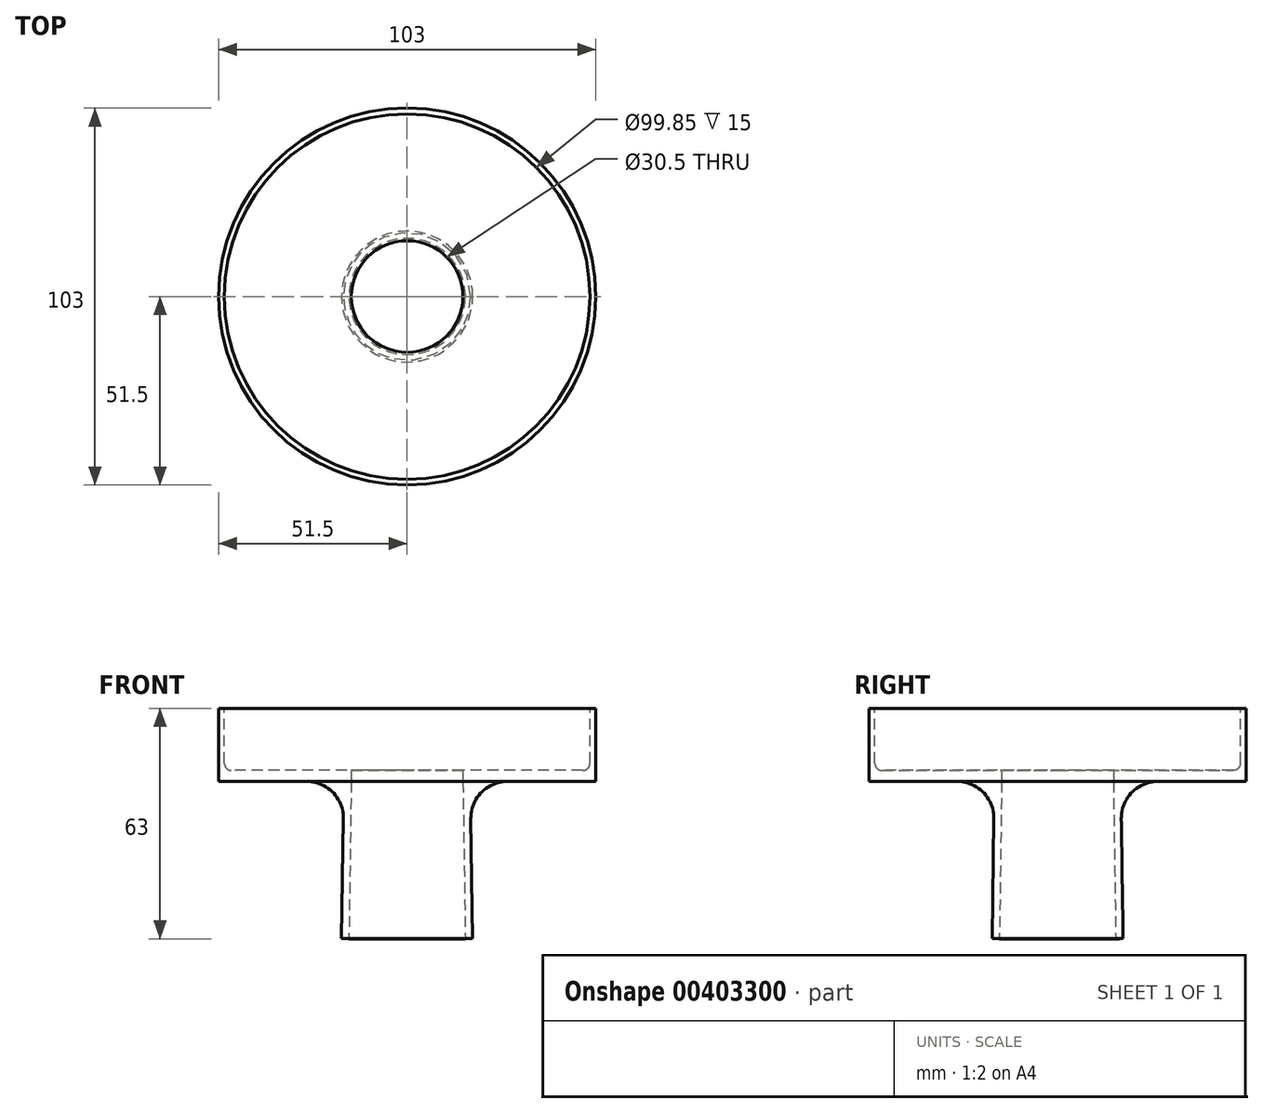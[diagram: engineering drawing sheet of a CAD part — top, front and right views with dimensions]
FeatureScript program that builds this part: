
annotation { "Feature Type Name" : "Feature", "Feature Type Description" : "" }
export const myFeature = defineFeature(function(context is Context, id is Id, definition is map)
    precondition{}
    {
        {
            var Q0;
            Q0=qCreatedBy(makeId("Top.planeOp"),FACE);
            var sketch = newSketch(context, id + "F0", { "sketchPlane" : qUnion([Q0])});
            skCircle(sketch, "E0", {"center": v(0, 0) * mm, "radius": 51.5 * mm});
            skSolve(sketch);
        }
        {
            var Q0;
            Q0 = qSketchRegion(id + "F0", true);
            extrude(context, id + "F1", {"entities" : qUnion([Q0]), "depth" : 20 * mm});
        }
        {
            var Q0;
            Q0=makeQuery(id+"F1.opExtrude","CAP_FACE",FACE,{"disambiguationData":[OSD([sQuery(id+"F0.wireOp",EDGE,"E0")])],"isStart":false});
            var sketch = newSketch(context, id + "F2", { "sketchPlane" : qUnion([Q0])});
            skCircle(sketch, "E1", {"center": v(0, 0) * mm, "radius": 49.92 * mm});
            skSolve(sketch);
        }
        {
            var Q0;
            Q0 = qSketchRegion(id + "F2", true);
            extrude(context, id + "F3", {"entities" : qUnion([Q0]), "operationType" : NewBodyOperationType.REMOVE, "oppositeDirection" : true, "depth" : 17 * mm});
        }
        {
            var Q0;
            Q0=makeQuery(id+"F1.opExtrude","CAP_FACE",FACE,{"disambiguationData":[OSD([sQuery(id+"F0.wireOp",EDGE,"E0")])],"isStart":true});
            var sketch = newSketch(context, id + "F4", { "sketchPlane" : qUnion([Q0])});
            skCircle(sketch, "E2", {"center": v(0, 0) * mm, "radius": 15.25 * mm});
            skSolve(sketch);
        }
        {
            var Q0;
            Q0 = qSketchRegion(id + "F4", true);
            extrude(context, id + "F5", {"entities" : qUnion([Q0]), "operationType" : NewBodyOperationType.REMOVE, "oppositeDirection" : true, "depth" : 25 * mm});
        }
        {
            var Q0;
            Q0=qCreatedBy(makeId("Right.planeOp"),FACE);
            var sketch = newSketch(context, id + "F6", { "sketchPlane" : qUnion([Q0])});
            skLineSegment(sketch, "E3", {"start": v(15.25, 0) * mm, "end": v(15.9, -43) * mm});
            skLineSegment(sketch, "E4.0", {"start": v(17.25, 0.03) * mm, "end": v(17.9, -42.97) * mm});
            skLineSegment(sketch, "E5", {"start": v(15.9, -43) * mm, "end": v(17.9, -42.97) * mm});
            skLineSegment(sketch, "E6", {"start": v(15.25, 0) * mm, "end": v(17.25, 0.03) * mm});
            skSolve(sketch);
        }
        {
            var Q0;
            Q0 = qSketchRegion(id + "F6", true);
            var Q1;
            Q1=makeQuery(id+"F1.opExtrude","CAP_EDGE",EDGE,{"disambiguationData":[OSD([sQuery(id+"F0.wireOp",EDGE,"E0")])],"isStart":true});
            sweep(context, id + "F7", {"operationType" : NewBodyOperationType.ADD, "profiles" : qUnion([Q0]), "path" : qUnion([Q1])});
        }
        {
            var Q0;
            {var subQ0=sQuery(id+"F0.wireOp",EDGE,"E0");Q0=makeQuery(id+"F7.boolean.opBoolean","INTERSECT",EDGE,{"derivedFrom":[makeQuery(id+"F1.opExtrude","CAP_FACE",FACE,{"disambiguationData":[OSD([subQ0])],"isStart":true}),makeQuery(id+"F7.opSweep","SWEPT_FACE",FACE,{"disambiguationData":[OSD([subQ0,sQuery(id+"F6.wireOp",EDGE,"E4.0")])]})]});}
            fillet(context, id + "F8", {"entities" : qUnion([Q0]), "radius" : 10 * mm, "tangentPropagation" : true, "allowEdgeOverflow" : false});
        }
        {
            var Q0;
            Q0=makeQuery(id+"F3.boolean.opBoolean","COPY",EDGE,{"derivedFrom":makeQuery(id+"F3.opExtrude","CAP_EDGE",EDGE,{"disambiguationData":[OSD([sQuery(id+"F2.wireOp",EDGE,"E1")])],"isStart":false})});
            fillet(context, id + "F9", {"entities" : qUnion([Q0]), "radius" : 2 * mm, "tangentPropagation" : true, "allowEdgeOverflow" : false});
        }
    });
